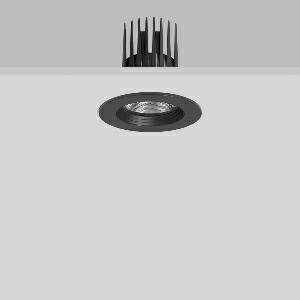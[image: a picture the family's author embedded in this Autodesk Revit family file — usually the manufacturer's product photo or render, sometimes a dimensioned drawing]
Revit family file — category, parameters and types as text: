
# Revit family: heledon_mini_e_901750_003_3_b0d2
name_source: partatom
category: Lighting Fixtures
units: mm (PartAtom-declared; Revit-internal decimal feet)

## family parameters
Cut with Voids When Loaded = No
Host = Face
Light Source = No
Part Type = Normal
Room Calculation Point = No
Round Connector Dimension = Use Diameter
Shared = No

## types (1)
- HELEDON mini E (1 x LED Modul 935, 3800 lm, 3500)
    Apparent Load = 29 VA
    Approval mark = CE
    CIE Flux Codes = 95 99 100 100 100
    Color Rendering = 92
    Color Temperature = 3500
    Default Elevation = 1800 mm
    Description = Series: HELEDON mini
Round recessed downlight. Housing: die-cast aluminium, powder-coated. Black plastic ring and recessed LED to prevent glare from the side. Optical assembly with reflector made of MIRO-Silver with 98% total light reflection for outstanding efficiency - can be changed without tools. Best colour rendering index Ra>90. Suitable for Recessed ceiling mounting. Installation without tools thanks to spring fastening system. Including separate LED converter with connecting cable 600 mm.High quality converter without flickering and stroboscopic effect. Through-wiring box (5 pole) available as accessory. The following accessories can be mounted without use of tools: interchangeable lenses, decorative glasses, honeycomb louvre, clear and frosted diffusers, white interchangeable plastic ring. 
Colour: deep black, matt (RAL 9005)
Diameter: 124 mm
Height: 3 mm
Cut-out diameter: 114 mm
Recess height: 170 mm
Luminaire: recess height: 120 mm
Lamp: LED
Socket: without socket
Colour temperature: 3500K
Colour rendering index (CRI): 92
System power: 29 W
Rated luminous flux: 3800 lm
Luminous efficiency: 131 lm/W
Control gear: Regulated power supply
Protection class: II
Type of protection: IP 20
    Height = 0 mm  [stored 0 ft]
    Lamp = 1 x LED Modul 935
    Lamp Light Flux = 3800 lm
    Lamp count = 1
    Length = 124 mm  [stored 0.406824 ft]
    Lifetime = 50000 h
    Luminous efficacy = 131 lm/W
    Manufacturer = RZB
    ModVariant = No
    Model = 901750.003.3
    Mounting Place = Ceiling
    Mounting Type = Recessed
    Number of Poles = 1
    OnlyDefault = Yes
    Power Factor = 1
    Product Name = HELEDON mini E
    Product group = Recessed downlights
    ProductGroupID = 402
    Protection Class = Protection class II
    Protection Degree = IP 20
    RLX_Detail_Level = 1
    RLX_Emergency_Light_Flux = 0 lm
    RLX_Emergency_Type = 0
    RLX_Emergency_Type_DB = No
    RlxData = <blob elided: 128081 chars, md5=7488d87e>
    Socket = socket
    Standby Power = 0 W
    System Light Flux = 3800 lm
    System Power = 29 W
    Type Comments = Product without accessories
    Type Image = 901657.003.jpg
    URL = http://relux.com
    VarID = ---
    Voltage = 230 V
    Voltage Range = 220-240 V
    Weight = 0.00 kg
    Width = 0 mm  [stored 0 ft]

note: [stored X ft] marks values corroborated as IEEE doubles in the binary element streams (Revit-internal decimal feet)

## geometry (parser evidence)
native form markers: Blend x4, Sweep x11
no freeform markers — native parametric forms only
